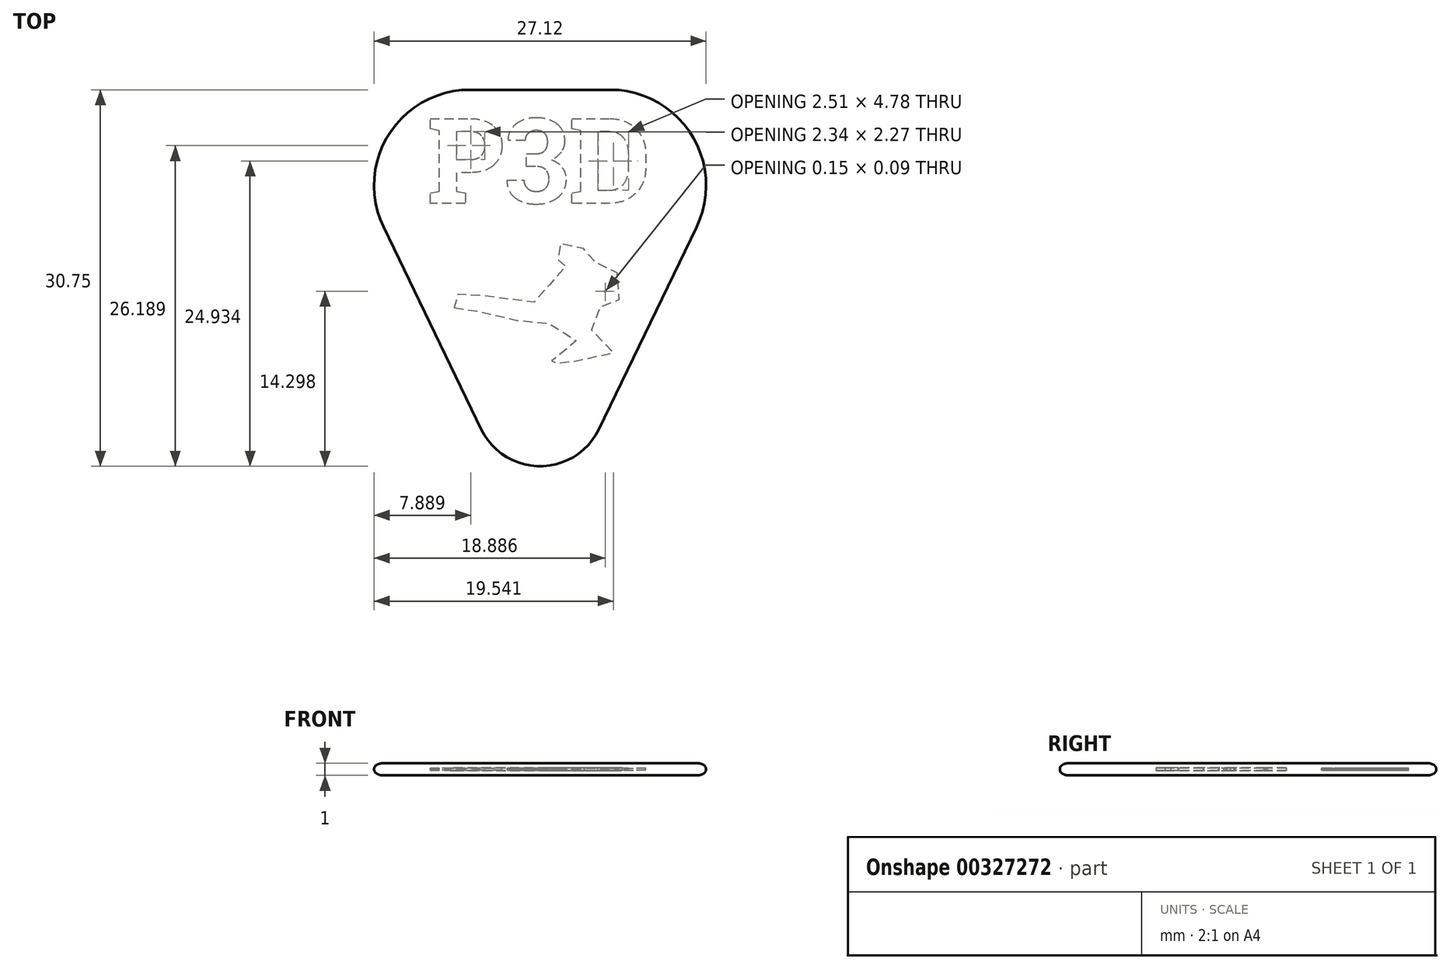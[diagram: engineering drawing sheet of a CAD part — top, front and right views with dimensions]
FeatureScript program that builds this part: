
annotation { "Feature Type Name" : "Feature", "Feature Type Description" : "" }
export const myFeature = defineFeature(function(context is Context, id is Id, definition is map)
    precondition{}
    {
        {
            var Q0;
            Q0=qCreatedBy(makeId("Top.planeOp"),FACE);
            var sketch = newSketch(context, id + "F0", { "sketchPlane" : qUnion([Q0])});
            skLineSegment(sketch, "E0", {"start": v(-5.74, 12.45) * mm, "end": v(5.74, 12.45) * mm});
            skLineSegment(sketch, "E1", {"start": v(12.95, 0.97) * mm, "end": v(4.95, -15.56) * mm});
            skLineSegment(sketch, "E2", {"start": v(-4.95, -15.56) * mm, "end": v(-12.95, 0.97) * mm});
            skPoint(sketch, "E3.visualSharp", {"position": v(-18.5, 12.45) * mm});
            skArc(sketch, "E3.filletArc", {"start": v(-5.74, 12.45) * mm, "mid": v(-12.52, 8.7) * mm, "end": v(-12.95, 0.97) * mm});
            skPoint(sketch, "E4.visualSharp", {"position": v(18.5, 12.45) * mm});
            skArc(sketch, "E4.filletArc", {"start": v(12.95, 0.97) * mm, "mid": v(12.52, 8.7) * mm, "end": v(5.74, 12.45) * mm});
            skPoint(sketch, "E5.visualSharp", {"position": v(0, -25.8) * mm});
            skArc(sketch, "E5.filletArc", {"start": v(-4.95, -15.56) * mm, "mid": v(0, -18.66) * mm, "end": v(4.95, -15.56) * mm});
            skSolve(sketch);
        }
        {
            var Q0;
            Q0=makeQuery(id+"F0.imprint","IMPRINT",FACE,{"disambiguationData":[TD([[makeQuery(id+"F0.imprint","IMPRINT",EDGE,{"derivedFrom":sQuery(id+"F0.wireOp",EDGE,"E0")}),-1.0]])]});
            extrude(context, id + "F1", {"entities" : qUnion([Q0]), "endBound" : BoundingType.SYMMETRIC, "depth" : 1 * mm, "offsetDistance" : 25 * mm});
        }
        {
            var Q0;
            Q0=makeQuery(id+"F1.opExtrude","CAP_EDGE",EDGE,{"disambiguationData":[OSD([sQuery(id+"F0.wireOp",EDGE,"E1")])],"isStart":false});
            var Q1;
            Q1=makeQuery(id+"F1.opExtrude","CAP_EDGE",EDGE,{"disambiguationData":[OSD([sQuery(id+"F0.wireOp",EDGE,"E1")])],"isStart":true});
            chamfer(context, id + "F2", {"entities" : qUnion([Q0, Q1]), "chamferType" : ChamferType.OFFSET_ANGLE, "width" : 0.5 * mm, "oppositeDirection" : false, "angle" : 45 * degree, "tangentPropagation" : true});
        }
        {
            var Q0;
            {var subQ0=sQuery(id+"F0.wireOp",EDGE,"E2");Q0=makeQuery(id+"F2.opChamfer","BLEND_EDGE",EDGE,{"blendedFrom":[makeQuery(id+"F1.opExtrude","CAP_EDGE",EDGE,{"disambiguationData":[OSD([subQ0])],"isStart":false}),makeQuery(id+"F1.opExtrude","CAP_FACE",FACE,{"disambiguationData":[OSD([sQuery(id+"F0.wireOp",EDGE,"E0"),sQuery(id+"F0.wireOp",EDGE,"E1"),subQ0,sQuery(id+"F0.wireOp",EDGE,"E3.filletArc"),sQuery(id+"F0.wireOp",EDGE,"E4.filletArc"),sQuery(id+"F0.wireOp",EDGE,"E5.filletArc")])],"isStart":false})],"blendedInto":[makeQuery(id+"F1.opExtrude","CAP_FACE",FACE,{"disambiguationData":[OSD([sQuery(id+"F0.wireOp",EDGE,"E0"),sQuery(id+"F0.wireOp",EDGE,"E1"),subQ0,sQuery(id+"F0.wireOp",EDGE,"E3.filletArc"),sQuery(id+"F0.wireOp",EDGE,"E4.filletArc"),sQuery(id+"F0.wireOp",EDGE,"E5.filletArc")])],"isStart":false})]});}
            var Q1;
            {var subQ0=sQuery(id+"F0.wireOp",EDGE,"E1");Q1=makeQuery(id+"F2.opChamfer","BLEND_EDGE",EDGE,{"blendedFrom":[makeQuery(id+"F1.opExtrude","CAP_EDGE",EDGE,{"disambiguationData":[OSD([subQ0])],"isStart":true}),makeQuery(id+"F1.opExtrude","CAP_FACE",FACE,{"disambiguationData":[OSD([sQuery(id+"F0.wireOp",EDGE,"E0"),subQ0,sQuery(id+"F0.wireOp",EDGE,"E2"),sQuery(id+"F0.wireOp",EDGE,"E3.filletArc"),sQuery(id+"F0.wireOp",EDGE,"E4.filletArc"),sQuery(id+"F0.wireOp",EDGE,"E5.filletArc")])],"isStart":true})],"blendedInto":[makeQuery(id+"F1.opExtrude","CAP_FACE",FACE,{"disambiguationData":[OSD([sQuery(id+"F0.wireOp",EDGE,"E0"),subQ0,sQuery(id+"F0.wireOp",EDGE,"E2"),sQuery(id+"F0.wireOp",EDGE,"E3.filletArc"),sQuery(id+"F0.wireOp",EDGE,"E4.filletArc"),sQuery(id+"F0.wireOp",EDGE,"E5.filletArc")])],"isStart":true})]});}
            fillet(context, id + "F3", {"entities" : qUnion([Q0, Q1]), "radius" : 1 * mm, "tangentPropagation" : true, "allowEdgeOverflow" : false});
        }
        {
            var Q0;
            Q0=qCreatedBy(makeId("Top.planeOp"),FACE);
            var sketch = newSketch(context, id + "F4", { "sketchPlane" : qUnion([Q0])});
            skText(sketch, "E6", { "text": "P3D", "fontName": "RobotoSlab-Bold.ttf"});
            const initialGuessF4  = {"E6": [-0.00923, 0.003, 1, 0, 0.007]};
            skSetInitialGuess(sketch, initialGuessF4);
            skSolve(sketch);
        }
        {
            var Q0;
            Q0=qSketchRegion(id+"F4",true);
            extrude(context, id + "F5", {"entities" : qUnion([Q0]), "operationType" : NewBodyOperationType.REMOVE, "endBound" : BoundingType.SYMMETRIC, "oppositeDirection" : true, "depth" : 0.18 * mm, "offsetDistance" : 25 * mm});
        }
        {
            var Q0;
            {var subQ0=sQuery(id+"F0.wireOp",EDGE,"E2");Q0=makeQuery(id+"F2.opChamfer","BLEND_EDGE",EDGE,{"blendedFrom":[makeQuery(id+"F1.opExtrude","CAP_EDGE",EDGE,{"disambiguationData":[OSD([subQ0])],"isStart":true}),makeQuery(id+"F1.opExtrude","CAP_EDGE",EDGE,{"disambiguationData":[OSD([subQ0])],"isStart":false})],"blendedInto":[]});}
            fillet(context, id + "F6", {"entities" : qUnion([Q0]), "radius" : 0.4 * mm, "tangentPropagation" : true, "allowEdgeOverflow" : false});
        }
        {
            var Q0;
            Q0=qCreatedBy(makeId("Top.planeOp"),FACE);
            var sketch = newSketch(context, id + "F7", { "sketchPlane" : qUnion([Q0])});
            skFitSpline(sketch, "E7", {"points": [v(-7.01, -5.53) * mm, v(-6.5, -5.48) * mm, v(-5.12, -5.72) * mm, v(-4.85, -5.95) * mm, v(-2.42, -6.48) * mm, v(-0.14, -6.78) * mm, v(0.71, -6.8) * mm, v(1.62, -7.52) * mm, v(3.1, -8.3) * mm, v(3.58, -8.54) * mm, v(2.97, -8.84) * mm, v(1.32, -8.84) * mm, v(1.26, -9.42) * mm, v(0.77, -10.08) * mm, v(0.63, -10.52) * mm, v(0.82, -10.63) * mm, v(1.87, -9.64) * mm, v(2.94, -9.5) * mm, v(3.02, -9.8) * mm, v(4.81, -9.64) * mm, v(6.13, -9.06) * mm, v(6.1, -8.43) * mm, v(3.63, -6.86) * mm, v(4.51, -5.93) * mm, v(5.3, -5.02) * mm, v(5.7, -4.93) * mm, v(6.4, -4.9) * mm, v(6.67, -4.53) * mm, v(6.52, -3.29) * mm, v(5.9, -2.06) * mm, v(5.13, -1.74) * mm, v(4.14, -1.83) * mm, v(3.76, -1.57) * mm, v(3.61, -1.03) * mm, v(3.24, -0.18) * mm, v(2.22, -0.05) * mm, v(1.4, -0.57) * mm, v(1.34, -1.15) * mm, v(1.3, -1.65) * mm, v(1.6, -1.56) * mm, v(1.65, -1.74) * mm, v(1.9, -1.74) * mm, v(1.98, -2.11) * mm, v(2.12, -2.18) * mm, v(2.12, -2.37) * mm, v(1.49, -2.75) * mm, v(0.59, -4.16) * mm, v(0.55, -4.7) * mm, v(-1.01, -5.1) * mm, v(-4.73, -4.57) * mm, v(-5.05, -4.78) * mm, v(-6.4, -4.65) * mm, v(-7.02, -4.27) * mm, v(-7.35, -4.82) * mm, v(-7.01, -5.53) * mm]});
            skFitSpline(sketch, "E8", {"points": [v(5.34, -4.14) * mm, v(5.25, -4.2) * mm, v(5.3, -4.23) * mm, v(5.4, -4.2) * mm, v(5.34, -4.14) * mm]});
            skSolve(sketch);
        }
        {
            var Q0;
            Q0=qSketchRegion(id+"F7",true);
            var Q1;
            Q1=makeQuery(id+"F7.imprint","IMPRINT",FACE,{"disambiguationData":[TD([[makeQuery(id+"F7.imprint","IMPRINT",EDGE,{"derivedFrom":sQuery(id+"F7.wireOp",EDGE,"939ed108-b3df-4f31-88ce-246f36476dcc.0")}),-1.0]])]});
            var Q2;
            Q2=makeQuery(id+"F7.imprint","IMPRINT",FACE,{"disambiguationData":[TD([[makeQuery(id+"F7.imprint","IMPRINT",EDGE,{"derivedFrom":sQuery(id+"F7.wireOp",EDGE,"7208b4ee-4551-4fd0-8a5f-77d057b4d0f6.0")}),-1.0]])]});
            extrude(context, id + "F8", {"entities" : qUnion([Q0, Q1, Q2]), "operationType" : NewBodyOperationType.REMOVE, "endBound" : BoundingType.SYMMETRIC, "depth" : 0.2 * mm, "offsetDistance" : 25 * mm});
        }
    });
